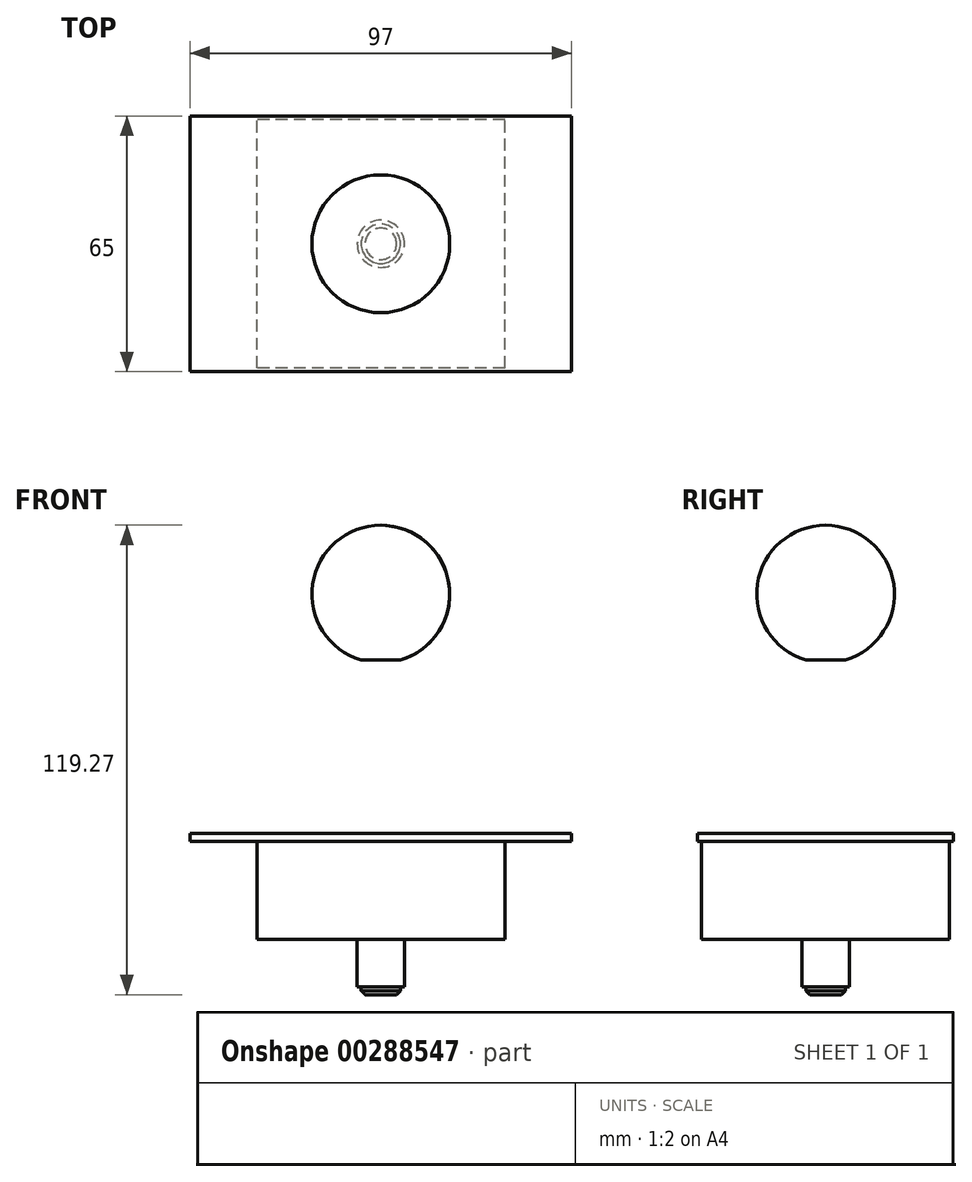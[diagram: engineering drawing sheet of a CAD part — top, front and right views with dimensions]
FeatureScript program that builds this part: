
annotation { "Feature Type Name" : "Feature", "Feature Type Description" : "" }
export const myFeature = defineFeature(function(context is Context, id is Id, definition is map)
    precondition{}
    {
        {
            var Q0;
            Q0=qCreatedBy(makeId("Front.planeOp"),FACE);
            var sketch = newSketch(context, id + "F0", { "sketchPlane" : qUnion([Q0])});
            skLineSegment(sketch, "E0.bottom", {"start": v(31.5, -12.5) * mm, "end": v(-31.5, -12.5) * mm});
            skLineSegment(sketch, "E0.top", {"start": v(31.5, 12.5) * mm, "end": v(-31.5, 12.5) * mm});
            skLineSegment(sketch, "E0.left", {"start": v(31.5, -12.5) * mm, "end": v(31.5, 12.5) * mm});
            skLineSegment(sketch, "E0.right", {"start": v(-31.5, -12.5) * mm, "end": v(-31.5, 12.5) * mm});
            skPoint(sketch, "E0.middle", {"position": v(0, 0) * mm});
            skLineSegment(sketch, "E1.bottom", {"start": v(48.5, 12.5) * mm, "end": v(-48.5, 12.5) * mm});
            skLineSegment(sketch, "E1.top", {"start": v(48.5, 14.5) * mm, "end": v(-48.5, 14.5) * mm});
            skLineSegment(sketch, "E1.left", {"start": v(48.5, 12.5) * mm, "end": v(48.5, 14.5) * mm});
            skLineSegment(sketch, "E1.right", {"start": v(-48.5, 12.5) * mm, "end": v(-48.5, 14.5) * mm});
            skPoint(sketch, "E1.middle", {"position": v(0, 13.5) * mm});
            skLineSegment(sketch, "E2.bottom", {"start": v(0, 14.5) * mm, "end": v(-5, 14.5) * mm});
            skLineSegment(sketch, "E2.top", {"start": v(0, 58.5) * mm, "end": v(-5, 58.5) * mm});
            skLineSegment(sketch, "E2.left", {"start": v(0, 14.5) * mm, "end": v(0, 58.5) * mm});
            skLineSegment(sketch, "E2.right", {"start": v(-5, 14.5) * mm, "end": v(-5, 58.5) * mm});
            skArc(sketch, "E3", {"start": v(-5, 58.5) * mm, "mid": v(-17.32, 77.8) * mm, "end": v(0, 92.77) * mm});
            skLineSegment(sketch, "E4", {"start": v(0, 92.77) * mm, "end": v(0, 58.5) * mm});
            skLineSegment(sketch, "E5", {"start": v(-6, -12.5) * mm, "end": v(-6, -24.5) * mm});
            skLineSegment(sketch, "E6", {"start": v(-6, -24.5) * mm, "end": v(-5, -24.5) * mm});
            skLineSegment(sketch, "E7", {"start": v(-5, -24.5) * mm, "end": v(-5, -26.5) * mm});
            skLineSegment(sketch, "E8", {"start": v(-5, -26.5) * mm, "end": v(0, -26.5) * mm});
            skLineSegment(sketch, "E9", {"start": v(0, -26.5) * mm, "end": v(0, -12.5) * mm});
            skLineSegment(sketch, "E10", {"start": v(0, -12.5) * mm, "end": v(-6, -12.5) * mm});
            skSolve(sketch);
        }
        {
            var Q0;
            Q0=makeQuery(id+"F0.imprint","IMPRINT",FACE,{"disambiguationData":[TD([[makeQuery(id+"F0.imprint","IMPRINT",EDGE,{"derivedFrom":sQuery(id+"F0.wireOp",EDGE,"E2.bottom")}),-1.0]])]});
            var Q1;
            Q1=makeQuery(id+"F0.imprint","IMPRINT",FACE,{"disambiguationData":[TD([[makeQuery(id+"F0.imprint","IMPRINT",EDGE,{"derivedFrom":sQuery(id+"F0.wireOp",EDGE,"E5")}),1.0]])]});
            var Q2;
            Q2=makeQuery(id+"F0.imprint","IMPRINT",FACE,{"disambiguationData":[TD([[makeQuery(id+"F0.imprint","IMPRINT",EDGE,{"derivedFrom":sQuery(id+"F0.wireOp",EDGE,"E2.top")}),-1.0]])]});
            var Q3;
            Q3=sQuery(id+"F0.wireOp",EDGE,"E4");
            revolve(context, id + "F1", {"entities" : qUnion([Q0, Q1, Q2]), "axis" : qUnion([Q3]), "revolveType" : RevolveType.FULL});
        }
        {
            var Q0;
            Q0=makeQuery(id+"F1.opRevolve","SWEPT_EDGE",EDGE,{"disambiguationData":[OSD([sQuery(id+"F0.wireOp",EDGE,"E7"),sQuery(id+"F0.wireOp",EDGE,"E8")])]});
            chamfer(context, id + "F2", {"entities" : qUnion([Q0]), "width" : 1 * mm, "tangentPropagation" : true});
        }
        {
            var Q0;
            {var subQ0=sQuery(id+"F0.wireOp",EDGE,"E1.left");Q0=makeQuery(id+"F0.imprint","IMPRINT",FACE,{"disambiguationData":[TD([[makeQuery(id+"F0.imprint","IMPRINT",EDGE,{"derivedFrom":subQ0}),1.0]])]});}
            extrude(context, id + "F3", {"entities" : qUnion([Q0]), "operationType" : NewBodyOperationType.ADD, "endBound" : BoundingType.SYMMETRIC, "depth" : 65 * mm});
        }
        {
            var Q0;
            {var subQ1=sQuery(id+"F0.wireOp",EDGE,"E0.left");Q0=makeQuery(id+"F0.imprint","IMPRINT",FACE,{"disambiguationData":[TD([[makeQuery(id+"F0.imprint","IMPRINT",EDGE,{"derivedFrom":subQ1}),1.0]])]});}
            extrude(context, id + "F4", {"entities" : qUnion([Q0]), "endBound" : BoundingType.SYMMETRIC, "depth" : 63 * mm});
        }
    });
